AUTODESK INVENTOR PART (.ipt)
format: ipt  version: 2022 (Build 260153000, 153)  size: 104,960 bytes
history: native  units: mm
features: sketch x2, extrude x1, fillet x1, projected_geometry x1
ambient origin geometry x8: Origin, YZ Plane, XZ Plane, XY Plane, X Axis, Y Axis, Z Axis, Center Point
bodies: Solid1 (feature_tree)
feature tree (5):
  extrude  "Extrusion1"  Depth=2.0mm
  fillet  "Fillet1"  Radius=2.0mm
  sketch  "Sketch2"  dims[d7=2.0mm d8=2.0mm d9=0.0mm d10=3.0mm d11=15.0mm d12=4.0mm]
  sketch  "Sketch1"  dims[d2=240.0mm d5=20.0mm d6=2.0mm]
  projected_geometry  "Projected Loop1"
